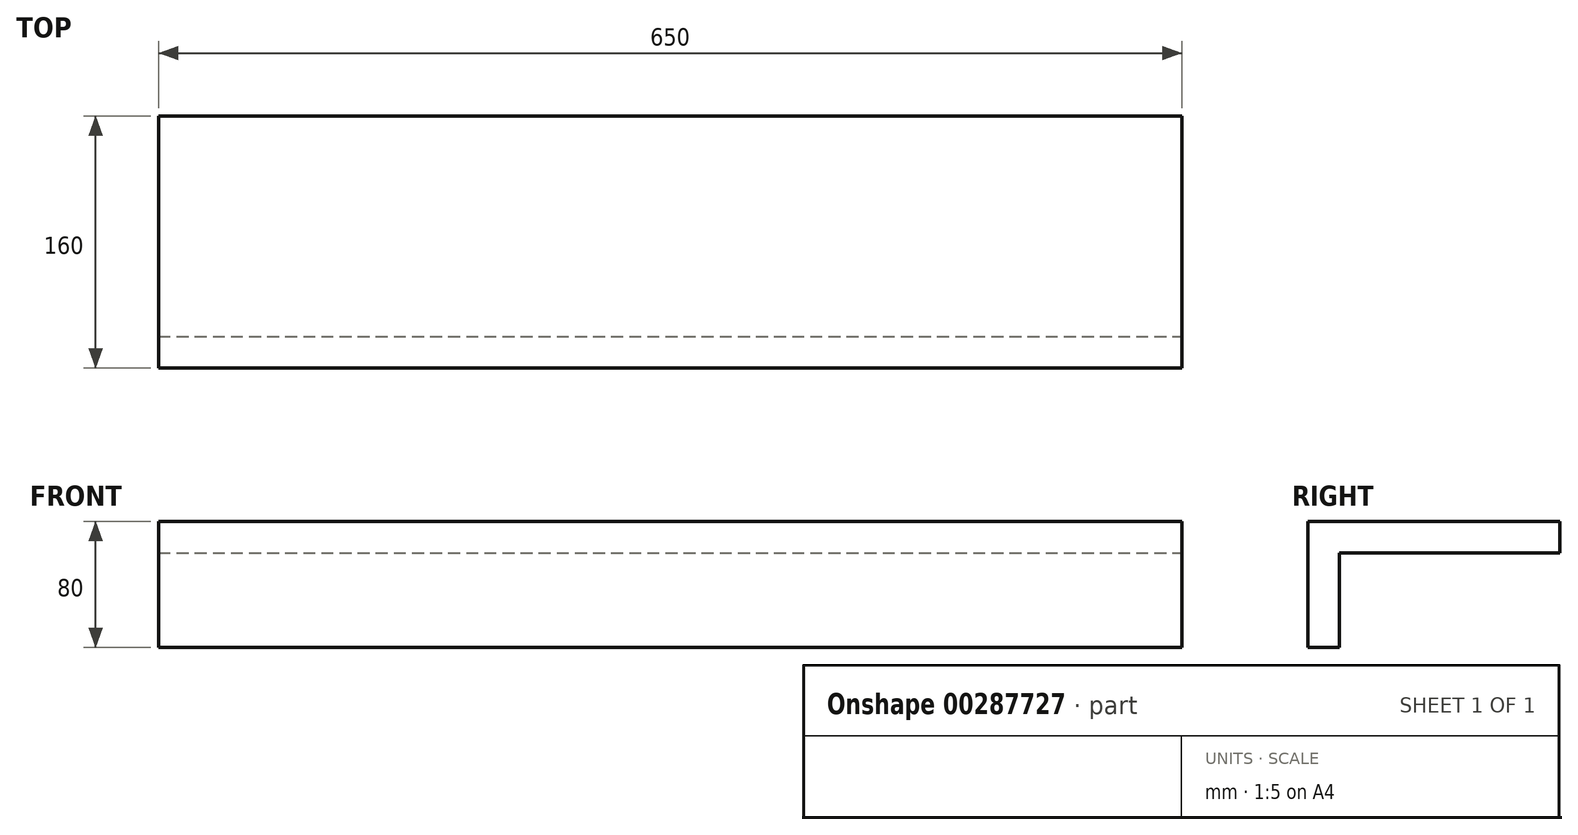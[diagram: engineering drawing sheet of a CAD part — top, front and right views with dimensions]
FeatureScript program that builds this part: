
annotation { "Feature Type Name" : "Feature", "Feature Type Description" : "" }
export const myFeature = defineFeature(function(context is Context, id is Id, definition is map)
    precondition{}
    {
        {
            var Q0;
            Q0=qCreatedBy(makeId("Top.planeOp"),FACE);
            var sketch = newSketch(context, id + "F0", { "sketchPlane" : qUnion([Q0])});
            skLineSegment(sketch, "E0.bottom", {"start": v(-205.6, 89.25) * mm, "end": v(444.4, 89.25) * mm});
            skLineSegment(sketch, "E0.top", {"start": v(-205.6, -70.75) * mm, "end": v(444.4, -70.75) * mm});
            skLineSegment(sketch, "E0.left", {"start": v(-205.6, 89.25) * mm, "end": v(-205.6, -70.75) * mm});
            skLineSegment(sketch, "E0.right", {"start": v(444.4, 89.25) * mm, "end": v(444.4, -70.75) * mm});
            skSolve(sketch);
        }
        {
            var Q0;
            Q0=makeQuery(id+"F0.imprint","IMPRINT",FACE,{"disambiguationData":[TD([[makeQuery(id+"F0.imprint","IMPRINT",EDGE,{"derivedFrom":sQuery(id+"F0.wireOp",EDGE,"E0.bottom")}),-1.0]])]});
            extrude(context, id + "F1", {"entities" : qUnion([Q0]), "depth" : 20 * mm});
        }
        {
            var Q0;
            Q0=makeQuery(id+"F1.opExtrude","CAP_FACE",FACE,{"disambiguationData":[OSD([sQuery(id+"F0.wireOp",EDGE,"E0.bottom"),sQuery(id+"F0.wireOp",EDGE,"E0.top"),sQuery(id+"F0.wireOp",EDGE,"E0.left"),sQuery(id+"F0.wireOp",EDGE,"E0.right")])],"isStart":true});
            var sketch = newSketch(context, id + "F2", { "sketchPlane" : qUnion([Q0])});
            skLineSegment(sketch, "E1", {"start": v(-205.6, 50.75) * mm, "end": v(444.4, 50.75) * mm});
            skSolve(sketch);
        }
        {
            var Q0;
            {var subQ0=sQuery(id+"F2.wireOp",EDGE,"E1");Q0=makeQuery(id+"F2.imprint","IMPRINT",FACE,{"disambiguationData":[TD([[makeQuery(id+"F2.imprint","IMPRINT",EDGE,{"derivedFrom":subQ0}),1.0]])]});}
            extrude(context, id + "F3", {"entities" : qUnion([Q0]), "operationType" : NewBodyOperationType.ADD, "depth" : 60 * mm});
        }
    });
